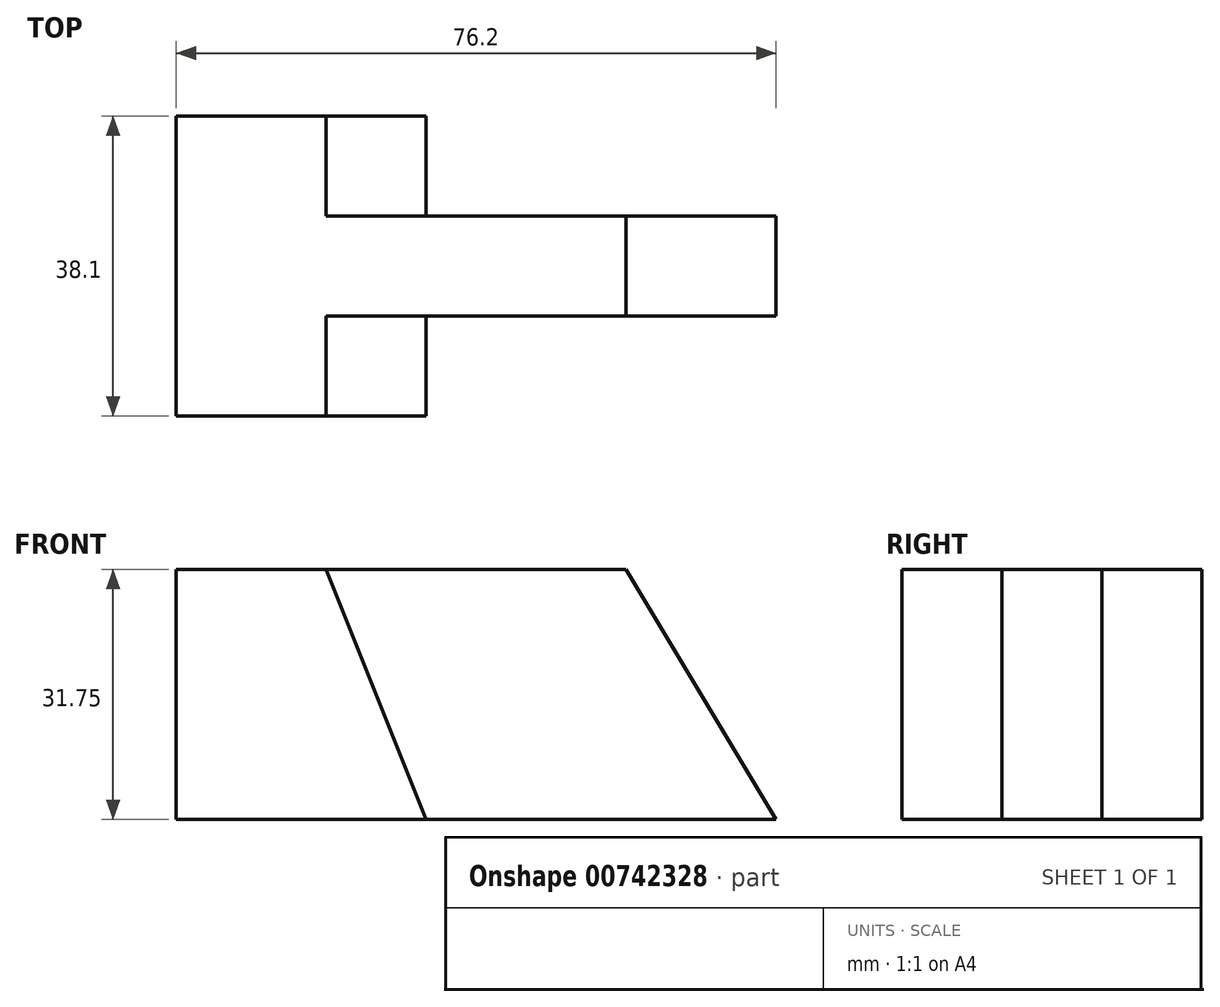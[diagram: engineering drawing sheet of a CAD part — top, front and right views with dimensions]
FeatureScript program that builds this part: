
annotation { "Feature Type Name" : "Feature", "Feature Type Description" : "" }
export const myFeature = defineFeature(function(context is Context, id is Id, definition is map)
    precondition{}
    {
        {
            var Q0;
            Q0=qCreatedBy(makeId("Front.planeOp"),FACE);
            var sketch = newSketch(context, id + "F0", { "sketchPlane" : qUnion([Q0])});
            skLineSegment(sketch, "E0", {"start": v(0, 0) * mm, "end": v(-31.75, 0) * mm});
            skLineSegment(sketch, "E1", {"start": v(-31.75, 0) * mm, "end": v(-31.75, 31.75) * mm});
            skLineSegment(sketch, "E2", {"start": v(-31.75, 31.75) * mm, "end": v(0, 31.75) * mm});
            skLineSegment(sketch, "E3", {"start": v(0, 31.75) * mm, "end": v(0, 0) * mm});
            skSolve(sketch);
        }
        {
            var Q0;
            Q0 = qSketchRegion(id + "F0", true);
            extrude(context, id + "F1", {"entities" : qUnion([Q0]), "depth" : 38.1 * mm, "offsetDistance" : 25.4 * mm});
        }
        {
            var Q0;
            Q0=makeQuery(id+"F1.opExtrude","SWEPT_FACE",FACE,{"disambiguationData":[OSD([sQuery(id+"F0.wireOp",EDGE,"E3")])]});
            var sketch = newSketch(context, id + "F2", { "sketchPlane" : qUnion([Q0])});
            skLineSegment(sketch, "E4", {"start": v(-25.4, 31.75) * mm, "end": v(-25.4, 0) * mm});
            skLineSegment(sketch, "E5", {"start": v(-25.4, 0) * mm, "end": v(-12.7, 0) * mm});
            skLineSegment(sketch, "E6", {"start": v(-12.7, 0) * mm, "end": v(-12.7, 31.75) * mm});
            skLineSegment(sketch, "E7", {"start": v(-12.7, 31.75) * mm, "end": v(-25.4, 31.75) * mm});
            skSolve(sketch);
        }
        {
            var Q0;
            Q0=makeQuery(id+"F2.imprint","IMPRINT",FACE,{"disambiguationData":[TD([[makeQuery(id+"F2.imprint","IMPRINT",EDGE,{"derivedFrom":sQuery(id+"F2.wireOp",EDGE,"E4")}),1.0]])]});
            extrude(context, id + "F3", {"entities" : qUnion([Q0]), "operationType" : NewBodyOperationType.ADD, "depth" : 44.45 * mm, "offsetDistance" : 25.4 * mm});
        }
        {
            var Q0;
            Q0=makeQuery(id+"F3.opExtrude","SWEPT_FACE",FACE,{"disambiguationData":[OSD([sQuery(id+"F2.wireOp",EDGE,"E4")])]});
            var sketch = newSketch(context, id + "F4", { "sketchPlane" : qUnion([Q0])});
            skLineSegment(sketch, "E8", {"start": v(25.4, 31.75) * mm, "end": v(44.45, 0) * mm});
            skLineSegment(sketch, "E9", {"start": v(44.45, 0) * mm, "end": v(44.45, 31.75) * mm});
            skLineSegment(sketch, "E10", {"start": v(44.45, 31.75) * mm, "end": v(25.4, 31.75) * mm});
            skSolve(sketch);
        }
        {
            var Q0;
            {var subQ0=sQuery(id+"F4.wireOp",EDGE,"E8");Q0=makeQuery(id+"F4.imprint","IMPRINT",FACE,{"disambiguationData":[TD([[makeQuery(id+"F4.imprint","IMPRINT",EDGE,{"derivedFrom":subQ0}),-1.0]])]});}
            var sketch = newSketch(context, id + "F5", { "sketchPlane" : qUnion([Q0])});
            skSolve(sketch);
        }
        {
            var Q0;
            Q0 = qSketchRegion(id + "F5", true);
            var Q1;
            Q1=makeQuery(id+"F4.imprint","IMPRINT",FACE,{"disambiguationData":[TD([[makeQuery(id+"F4.imprint","IMPRINT",EDGE,{"derivedFrom":sQuery(id+"F4.wireOp",EDGE,"E8")}),1.0]])]});
            extrude(context, id + "F6", {"entities" : qUnion([Q0, Q1]), "operationType" : NewBodyOperationType.REMOVE, "endBound" : BoundingType.THROUGH_ALL, "oppositeDirection" : true, "depth" : 25.4 * mm, "offsetDistance" : 25.4 * mm});
        }
        {
            var Q0;
            Q0=makeQuery(id+"F1.opExtrude","CAP_FACE",FACE,{"disambiguationData":[OSD([sQuery(id+"F0.wireOp",EDGE,"E0"),sQuery(id+"F0.wireOp",EDGE,"E1"),sQuery(id+"F0.wireOp",EDGE,"E2"),sQuery(id+"F0.wireOp",EDGE,"E3")])],"isStart":false});
            var sketch = newSketch(context, id + "F7", { "sketchPlane" : qUnion([Q0])});
            skLineSegment(sketch, "E11", {"start": v(0, 0) * mm, "end": v(0, 31.75) * mm});
            skLineSegment(sketch, "E12", {"start": v(0, 31.75) * mm, "end": v(-12.7, 31.75) * mm});
            skLineSegment(sketch, "E13", {"start": v(-12.7, 31.75) * mm, "end": v(0, 0) * mm});
            skSolve(sketch);
        }
        {
            var Q0;
            Q0 = qSketchRegion(id + "F7", true);
            extrude(context, id + "F8", {"entities" : qUnion([Q0]), "operationType" : NewBodyOperationType.REMOVE, "oppositeDirection" : true, "depth" : 12.7 * mm, "offsetDistance" : 25.4 * mm});
        }
        {
            var Q0;
            Q0=makeQuery(id+"F1.opExtrude","CAP_FACE",FACE,{"disambiguationData":[OSD([sQuery(id+"F0.wireOp",EDGE,"E0"),sQuery(id+"F0.wireOp",EDGE,"E1"),sQuery(id+"F0.wireOp",EDGE,"E2"),sQuery(id+"F0.wireOp",EDGE,"E3")])],"isStart":true});
            var sketch = newSketch(context, id + "F9", { "sketchPlane" : qUnion([Q0])});
            skLineSegment(sketch, "E14", {"start": v(0, 0) * mm, "end": v(0, 31.75) * mm});
            skLineSegment(sketch, "E15", {"start": v(0, 31.75) * mm, "end": v(12.7, 31.75) * mm});
            skLineSegment(sketch, "E16", {"start": v(12.7, 31.75) * mm, "end": v(0, 0) * mm});
            skSolve(sketch);
        }
        {
            var Q0;
            Q0 = qSketchRegion(id + "F9", true);
            extrude(context, id + "F10", {"entities" : qUnion([Q0]), "operationType" : NewBodyOperationType.REMOVE, "oppositeDirection" : true, "depth" : 12.7 * mm, "offsetDistance" : 25.4 * mm});
        }
    });
